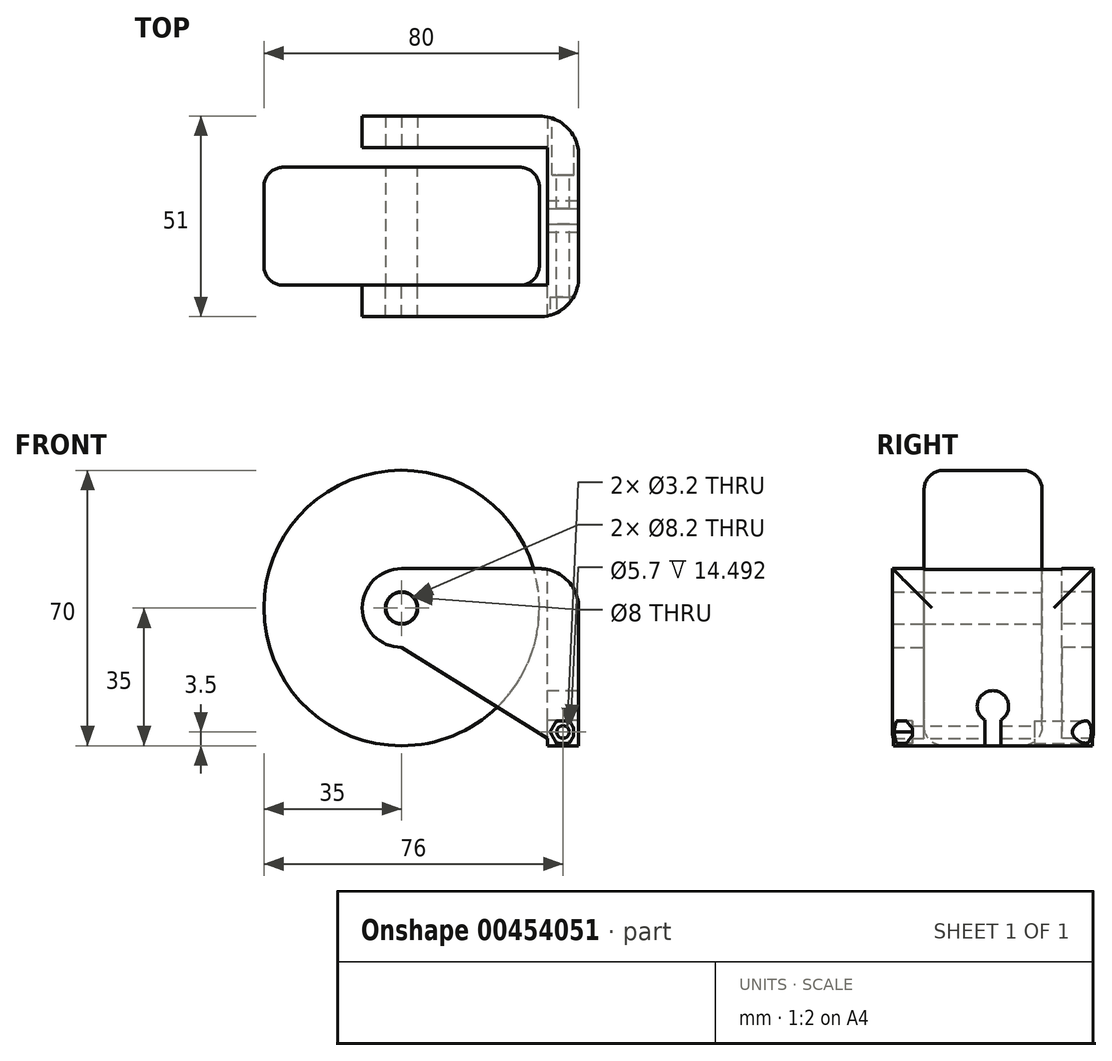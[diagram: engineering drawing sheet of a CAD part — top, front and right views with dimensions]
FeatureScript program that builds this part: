
annotation { "Feature Type Name" : "Feature", "Feature Type Description" : "" }
export const myFeature = defineFeature(function(context is Context, id is Id, definition is map)
    precondition{}
    {
        {
            var Q0;
            Q0=qCreatedBy(makeId("Front.planeOp"),FACE);
            var sketch = newSketch(context, id + "F0", { "sketchPlane" : qUnion([Q0])});
            skCircle(sketch, "E0", {"center": v(0, 0) * mm, "radius": 35 * mm});
            skCircle(sketch, "E1", {"center": v(0, 0) * mm, "radius": 4 * mm});
            skSolve(sketch);
        }
        {
            var Q0;
            Q0 = qSketchRegion(id + "F0", true);
            extrude(context, id + "F1", {"entities" : qUnion([Q0]), "depth" : 30 * mm, "offsetDistance" : 25 * mm});
        }
        {
            var Q0;
            Q0=makeQuery(id+"F1.opExtrude","CAP_EDGE",EDGE,{"disambiguationData":[OSD([sQuery(id+"F0.wireOp",EDGE,"E0")])],"isStart":false});
            var Q1;
            Q1=makeQuery(id+"F1.opExtrude","CAP_EDGE",EDGE,{"disambiguationData":[OSD([sQuery(id+"F0.wireOp",EDGE,"E0")])],"isStart":true});
            fillet(context, id + "F2", {"entities" : qUnion([Q0, Q1]), "tangentPropagation" : true, "radius" : 5 * mm, "defaultsChanged" : false, "vertexSettings" : [], "allowEdgeOverflow" : false});
        }
        {
            var Q0;
            Q0=makeQuery(id+"F1.opExtrude","CAP_FACE",FACE,{"disambiguationData":[OSD([sQuery(id+"F0.wireOp",EDGE,"E0"),sQuery(id+"F0.wireOp",EDGE,"E1")])],"isStart":false});
            var sketch = newSketch(context, id + "F3", { "sketchPlane" : qUnion([Q0])});
            skLineSegment(sketch, "E2", {"start": v(0, 10) * mm, "end": v(45, 10) * mm});
            skLineSegment(sketch, "E3", {"start": v(45, 10) * mm, "end": v(45, -35) * mm});
            skLineSegment(sketch, "E4", {"start": v(45, -35) * mm, "end": v(40, -35) * mm});
            skLineSegment(sketch, "E5", {"start": v(0, 10) * mm, "end": v(-10, 10) * mm});
            skLineSegment(sketch, "E6", {"start": v(-10, 10) * mm, "end": v(-10, -10) * mm});
            skLineSegment(sketch, "E7", {"start": v(-10, -10) * mm, "end": v(0, -10) * mm});
            skLineSegment(sketch, "E8", {"start": v(0, -10) * mm, "end": v(40, -35) * mm});
            skCircle(sketch, "E9", {"center": v(0, 0) * mm, "radius": 4.1 * mm});
            skSolve(sketch);
        }
        {
            var Q0;
            Q0 = qSketchRegion(id + "F3", true);
            extrude(context, id + "F4", {"entities" : qUnion([Q0]), "depth" : 8 * mm, "offsetDistance" : 25 * mm});
        }
        {
            var Q0;
            Q0=makeQuery(id+"F4.opExtrude","SWEPT_BODY",BODY,{"disambiguationData":[OSD([sQuery(id+"F3.wireOp",EDGE,"E2"),sQuery(id+"F3.wireOp",EDGE,"E3"),sQuery(id+"F3.wireOp",EDGE,"E4"),sQuery(id+"F3.wireOp",EDGE,"E5"),sQuery(id+"F3.wireOp",EDGE,"E6"),sQuery(id+"F3.wireOp",EDGE,"E7"),sQuery(id+"F3.wireOp",EDGE,"E8"),sQuery(id+"F3.wireOp",EDGE,"E9")])]});
            var Q1;
            Q1=makeQuery(id+"F4.opExtrude","CAP_FACE",FACE,{"disambiguationData":[OSD([sQuery(id+"F3.wireOp",EDGE,"E2"),sQuery(id+"F3.wireOp",EDGE,"E3"),sQuery(id+"F3.wireOp",EDGE,"E4"),sQuery(id+"F3.wireOp",EDGE,"E5"),sQuery(id+"F3.wireOp",EDGE,"E6"),sQuery(id+"F3.wireOp",EDGE,"E7"),sQuery(id+"F3.wireOp",EDGE,"E8"),sQuery(id+"F3.wireOp",EDGE,"E9")])],"isStart":true});
            mirror(context, id + "F5", {"entities" : qUnion([Q0]), "mirrorPlane" : qUnion([Q1])});
        }
        {
            var Q0;
            Q0=makeQuery(id+"F5.opPattern","COPY",BODY,{"derivedFrom":makeQuery(id+"F4.opExtrude","SWEPT_BODY",BODY,{"disambiguationData":[OSD([sQuery(id+"F3.wireOp",EDGE,"E2"),sQuery(id+"F3.wireOp",EDGE,"E3"),sQuery(id+"F3.wireOp",EDGE,"E4"),sQuery(id+"F3.wireOp",EDGE,"E5"),sQuery(id+"F3.wireOp",EDGE,"E6"),sQuery(id+"F3.wireOp",EDGE,"E7"),sQuery(id+"F3.wireOp",EDGE,"E8"),sQuery(id+"F3.wireOp",EDGE,"E9")])]}),"instanceName":"1"});
            transform(context, id + "F6", {"entities" : qUnion([Q0]), "transformType" : TransformType.TRANSLATION_3D, "dx" : 0 * mm, "dy" : 35 * mm, "dz" : 0 * mm, "makeCopy" : false});
        }
        {
            var Q0;
            Q0=makeQuery(id+"F4.opExtrude","SWEPT_FACE",FACE,{"disambiguationData":[OSD([sQuery(id+"F3.wireOp",EDGE,"E3")])]});
            var sketch = newSketch(context, id + "F7", { "sketchPlane" : qUnion([Q0])});
            skLineSegment(sketch, "E10", {"start": v(-38, 10) * mm, "end": v(13, 10) * mm});
            skLineSegment(sketch, "E11", {"start": v(13, 10) * mm, "end": v(13, -35) * mm});
            skLineSegment(sketch, "E12", {"start": v(13, -35) * mm, "end": v(-38, -35) * mm});
            skLineSegment(sketch, "E13", {"start": v(-38, -35) * mm, "end": v(-38, 10) * mm});
            skSolve(sketch);
        }
        {
            var Q0;
            Q0 = qSketchRegion(id + "F7", true);
            extrude(context, id + "F8", {"entities" : qUnion([Q0]), "oppositeDirection" : true, "depth" : 8 * mm, "offsetDistance" : 25 * mm});
        }
        {
            var Q0;
            Q0=makeQuery(id+"F4.opExtrude","SWEPT_BODY",BODY,{"disambiguationData":[OSD([sQuery(id+"F3.wireOp",EDGE,"E2"),sQuery(id+"F3.wireOp",EDGE,"E3"),sQuery(id+"F3.wireOp",EDGE,"E4"),sQuery(id+"F3.wireOp",EDGE,"E5"),sQuery(id+"F3.wireOp",EDGE,"E6"),sQuery(id+"F3.wireOp",EDGE,"E7"),sQuery(id+"F3.wireOp",EDGE,"E8"),sQuery(id+"F3.wireOp",EDGE,"E9")])]});
            var Q1;
            Q1=makeQuery(id+"F8.opExtrude","SWEPT_BODY",BODY,{"disambiguationData":[OSD([sQuery(id+"F7.wireOp",EDGE,"E10"),sQuery(id+"F7.wireOp",EDGE,"E11"),sQuery(id+"F7.wireOp",EDGE,"E12"),sQuery(id+"F7.wireOp",EDGE,"E13")])]});
            var Q2;
            Q2=makeQuery(id+"F5.opPattern","COPY",BODY,{"derivedFrom":makeQuery(id+"F4.opExtrude","SWEPT_BODY",BODY,{"disambiguationData":[OSD([sQuery(id+"F3.wireOp",EDGE,"E2"),sQuery(id+"F3.wireOp",EDGE,"E3"),sQuery(id+"F3.wireOp",EDGE,"E4"),sQuery(id+"F3.wireOp",EDGE,"E5"),sQuery(id+"F3.wireOp",EDGE,"E6"),sQuery(id+"F3.wireOp",EDGE,"E7"),sQuery(id+"F3.wireOp",EDGE,"E8"),sQuery(id+"F3.wireOp",EDGE,"E9")])]}),"instanceName":"1"});
            booleanBodies(context, id + "F9", {"operationType" : BooleanOperationType.UNION, "tools" : qUnion([Q0, Q1, Q2])});
        }
        {
            var Q0;
            Q0=makeQuery(id+"F9.opBoolean","MERGE",FACE,{"derivedFrom":[makeQuery(id+"F4.opExtrude","SWEPT_FACE",FACE,{"disambiguationData":[OSD([sQuery(id+"F3.wireOp",EDGE,"E3")])]}),makeQuery(id+"F8.opExtrude","CAP_FACE",FACE,{"disambiguationData":[OSD([sQuery(id+"F7.wireOp",EDGE,"E10"),sQuery(id+"F7.wireOp",EDGE,"E11"),sQuery(id+"F7.wireOp",EDGE,"E12"),sQuery(id+"F7.wireOp",EDGE,"E13")])],"isStart":true})]});
            var sketch = newSketch(context, id + "F10", { "sketchPlane" : qUnion([Q0])});
            skPoint(sketch, "E14.centerSnap0", {"position": v(-12.5, -35) * mm});
            skLineSegment(sketch, "E15.bottom", {"start": v(-12.5, -35) * mm, "end": v(-14.5, -35) * mm});
            skLineSegment(sketch, "E15.left", {"start": v(-10.5, -35) * mm, "end": v(-10.5, -28.46) * mm});
            skLineSegment(sketch, "E15.right", {"start": v(-14.5, -35) * mm, "end": v(-14.5, -28.46) * mm});
            skArc(sketch, "E16", {"start": v(-10.5, -28.46) * mm, "mid": v(-12.5, -21) * mm, "end": v(-14.5, -28.46) * mm});
            skLineSegment(sketch, "E17", {"start": v(-10.5, -35) * mm, "end": v(-12.5, -35) * mm});
            skSolve(sketch);
        }
        {
            var Q0;
            Q0 = qSketchRegion(id + "F10", true);
            extrude(context, id + "F11", {"entities" : qUnion([Q0]), "operationType" : NewBodyOperationType.REMOVE, "oppositeDirection" : true, "depth" : 8 * mm, "offsetDistance" : 25 * mm});
        }
        {
            var Q0;
            Q0=makeQuery(id+"F9.opBoolean","MERGE",FACE,{"derivedFrom":[makeQuery(id+"F5.opPattern","COPY",FACE,{"derivedFrom":makeQuery(id+"F4.opExtrude","CAP_FACE",FACE,{"disambiguationData":[OSD([sQuery(id+"F3.wireOp",EDGE,"E2"),sQuery(id+"F3.wireOp",EDGE,"E3"),sQuery(id+"F3.wireOp",EDGE,"E4"),sQuery(id+"F3.wireOp",EDGE,"E5"),sQuery(id+"F3.wireOp",EDGE,"E6"),sQuery(id+"F3.wireOp",EDGE,"E7"),sQuery(id+"F3.wireOp",EDGE,"E8"),sQuery(id+"F3.wireOp",EDGE,"E9")])],"isStart":false}),"instanceName":"1"}),makeQuery(id+"F8.opExtrude","SWEPT_FACE",FACE,{"disambiguationData":[OSD([sQuery(id+"F7.wireOp",EDGE,"E11")])]})]});
            var sketch = newSketch(context, id + "F12", { "sketchPlane" : qUnion([Q0])});
            skCircle(sketch, "E18", {"center": v(-41, -31.5) * mm, "radius": 1.6 * mm});
            skPoint(sketch, "E18.centerSnap0", {"position": v(-41, -35) * mm});
            skSolve(sketch);
        }
        {
            var Q0;
            Q0 = qSketchRegion(id + "F12", true);
            extrude(context, id + "F13", {"entities" : qUnion([Q0]), "operationType" : NewBodyOperationType.REMOVE, "oppositeDirection" : true, "depth" : 51 * mm, "offsetDistance" : 25 * mm});
        }
        {
            var Q0;
            Q0=makeQuery(id+"F9.opBoolean","MERGE",FACE,{"derivedFrom":[makeQuery(id+"F5.opPattern","COPY",FACE,{"derivedFrom":makeQuery(id+"F4.opExtrude","CAP_FACE",FACE,{"disambiguationData":[OSD([sQuery(id+"F3.wireOp",EDGE,"E2"),sQuery(id+"F3.wireOp",EDGE,"E3"),sQuery(id+"F3.wireOp",EDGE,"E4"),sQuery(id+"F3.wireOp",EDGE,"E5"),sQuery(id+"F3.wireOp",EDGE,"E6"),sQuery(id+"F3.wireOp",EDGE,"E7"),sQuery(id+"F3.wireOp",EDGE,"E8"),sQuery(id+"F3.wireOp",EDGE,"E9")])],"isStart":false}),"instanceName":"1"}),makeQuery(id+"F8.opExtrude","SWEPT_FACE",FACE,{"disambiguationData":[OSD([sQuery(id+"F7.wireOp",EDGE,"E11")])]})]});
            var sketch = newSketch(context, id + "F14", { "sketchPlane" : qUnion([Q0])});
            skCircle(sketch, "E19", {"center": v(-41, -31.5) * mm, "radius": 2.85 * mm});
            skSolve(sketch);
        }
        {
            var Q0;
            Q0 = qSketchRegion(id + "F14", true);
            extrude(context, id + "F15", {"entities" : qUnion([Q0]), "operationType" : NewBodyOperationType.REMOVE, "oppositeDirection" : true, "depth" : 15 * mm, "offsetDistance" : 25 * mm});
        }
        {
            var Q0;
            Q0=makeQuery(id+"F9.opBoolean","MERGE",FACE,{"derivedFrom":[makeQuery(id+"F4.opExtrude","CAP_FACE",FACE,{"disambiguationData":[OSD([sQuery(id+"F3.wireOp",EDGE,"E2"),sQuery(id+"F3.wireOp",EDGE,"E3"),sQuery(id+"F3.wireOp",EDGE,"E4"),sQuery(id+"F3.wireOp",EDGE,"E5"),sQuery(id+"F3.wireOp",EDGE,"E6"),sQuery(id+"F3.wireOp",EDGE,"E7"),sQuery(id+"F3.wireOp",EDGE,"E8"),sQuery(id+"F3.wireOp",EDGE,"E9")])],"isStart":false}),makeQuery(id+"F8.opExtrude","SWEPT_FACE",FACE,{"disambiguationData":[OSD([sQuery(id+"F7.wireOp",EDGE,"E13")])]})]});
            var sketch = newSketch(context, id + "F16", { "sketchPlane" : qUnion([Q0])});
            skCircle(sketch, "E20.cCircle", {"center": v(41, -31.5) * mm, "radius": 2.85 * mm, "construction": true});
            skLineSegment(sketch, "E20.0", {"start": v(39.35, -28.65) * mm, "end": v(42.65, -28.65) * mm});
            skLineSegment(sketch, "E20.1", {"start": v(42.65, -28.65) * mm, "end": v(44.3, -31.5) * mm});
            skLineSegment(sketch, "E20.2", {"start": v(44.3, -31.5) * mm, "end": v(42.65, -34.35) * mm});
            skLineSegment(sketch, "E20.3", {"start": v(42.65, -34.35) * mm, "end": v(39.35, -34.35) * mm});
            skLineSegment(sketch, "E20.4", {"start": v(39.35, -34.35) * mm, "end": v(37.7, -31.5) * mm});
            skLineSegment(sketch, "E20.5", {"start": v(37.7, -31.5) * mm, "end": v(39.35, -28.65) * mm});
            skPoint(sketch, "E20.0.midPoint", {"position": v(41, -28.65) * mm});
            skSolve(sketch);
        }
        {
            var Q0;
            Q0 = qSketchRegion(id + "F16", true);
            extrude(context, id + "F17", {"entities" : qUnion([Q0]), "operationType" : NewBodyOperationType.REMOVE, "oppositeDirection" : true, "depth" : 5 * mm, "offsetDistance" : 25 * mm});
        }
        {
            var Q0;
            Q0=makeQuery(id+"F4.opExtrude","SWEPT_EDGE",EDGE,{"disambiguationData":[OSD([sQuery(id+"F3.wireOp",EDGE,"E6"),sQuery(id+"F3.wireOp",EDGE,"E7")])]});
            var Q1;
            Q1=makeQuery(id+"F4.opExtrude","SWEPT_EDGE",EDGE,{"disambiguationData":[OSD([sQuery(id+"F3.wireOp",EDGE,"E5"),sQuery(id+"F3.wireOp",EDGE,"E6")])]});
            var Q2;
            Q2=makeQuery(id+"F5.opPattern","COPY",EDGE,{"derivedFrom":makeQuery(id+"F4.opExtrude","SWEPT_EDGE",EDGE,{"disambiguationData":[OSD([sQuery(id+"F3.wireOp",EDGE,"E6"),sQuery(id+"F3.wireOp",EDGE,"E7")])]}),"instanceName":"1"});
            var Q3;
            Q3=makeQuery(id+"F5.opPattern","COPY",EDGE,{"derivedFrom":makeQuery(id+"F4.opExtrude","SWEPT_EDGE",EDGE,{"disambiguationData":[OSD([sQuery(id+"F3.wireOp",EDGE,"E5"),sQuery(id+"F3.wireOp",EDGE,"E6")])]}),"instanceName":"1"});
            var Q4;
            Q4=makeQuery(id+"F9.opBoolean","MERGE",EDGE,{"derivedFrom":[makeQuery(id+"F4.opExtrude","SWEPT_EDGE",EDGE,{"disambiguationData":[OSD([sQuery(id+"F3.wireOp",EDGE,"E2"),sQuery(id+"F3.wireOp",EDGE,"E3")])]}),makeQuery(id+"F8.opExtrude","CAP_EDGE",EDGE,{"disambiguationData":[OSD([sQuery(id+"F7.wireOp",EDGE,"E10")])],"isStart":true})]});
            var Q5;
            Q5=makeQuery(id+"F8.opExtrude","CAP_EDGE",EDGE,{"disambiguationData":[OSD([sQuery(id+"F7.wireOp",EDGE,"E11")])],"isStart":true});
            var Q6;
            Q6=makeQuery(id+"F4.opExtrude","CAP_EDGE",EDGE,{"disambiguationData":[OSD([sQuery(id+"F3.wireOp",EDGE,"E3")])],"isStart":false});
            fillet(context, id + "F18", {"entities" : qUnion([Q0, Q1, Q2, Q3, Q4, Q5, Q6]), "tangentPropagation" : true, "radius" : 10 * mm, "defaultsChanged" : false, "vertexSettings" : [], "allowEdgeOverflow" : false});
        }
    });
